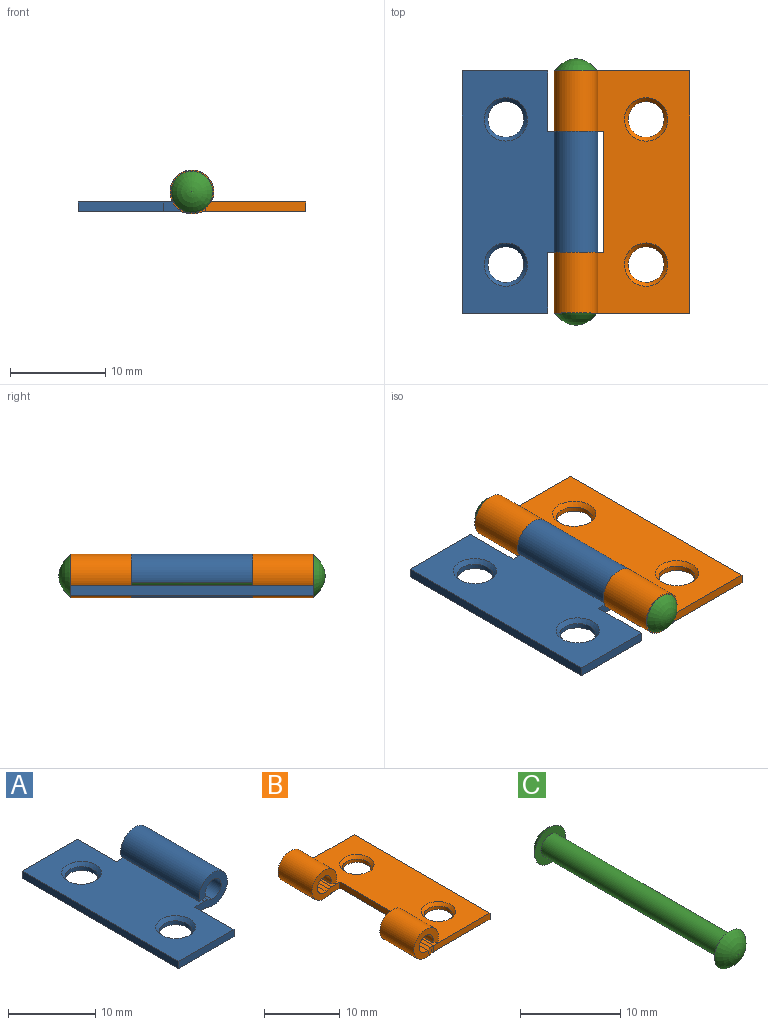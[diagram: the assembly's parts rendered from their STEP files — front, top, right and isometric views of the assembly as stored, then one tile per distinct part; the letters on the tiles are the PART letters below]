
ASSEMBLY  parts=3 mates=2
PART A: 20 faces, bbox 14.2x25.4x4.6 mm
  f0: cylinder r=2.3mm len=12.7mm, axis (0,1,0), area 154.7mm2, adj f1,f8,f13,f14
  f1: plane 12.7x0.95mm, normal (0.32,0,-0.95), area 12.7mm2, adj f0,f2,f13,f14
  f2: cylinder r=1.3mm len=12.7mm, axis (0,1,0), area 87.4mm2, adj f1,f3,f13,f14
  f3: plane 12.7x0.51mm, normal (0.26,0,0.97), area 6.7mm2, adj f2,f4,f13,f14
  f4: cylinder r=2.13mm len=12.7mm, axis (0,1,0), area 7.1mm2, adj f3,f5,f13,f14
  f5: plane 25.4x10.53mm, normal (0,0,1), area 214.9mm2, adj f4,f9,f10,f11,f12,f13,f14,f15
  f6: plane 25.4x10.53mm, normal (0,0,-1), area 225.2mm2, adj f7,f9,f10,f11,f12,f13,f14,f15
  f7: cylinder r=1.13mm len=12.7mm, axis (0,1,0), area 3.8mm2, adj f6,f8,f13,f14
  f8: plane 12.7x0.51mm, normal (-0.26,0,-0.97), area 6.7mm2, adj f0,f7,f13,f14
  f9: plane 8.95x1mm, normal (0,-1,0), area 8.9mm2, adj f5,f6,f11,f15
  f10: plane 8.95x1mm, normal (0,1,0), area 8.9mm2, adj f5,f6,f11,f12
  f11: plane 25.4x1mm, normal (-1,0,0), area 25.4mm2, adj f5,f6,f9,f10
  f12: plane 6.35x1mm, normal (1,0,0), area 6.3mm2, adj f5,f6,f10,f13
  f13: plane 5.28x4.6mm, normal (0,1,0), area 12.1mm2, adj f0,f1,f2,f3,f4,f5,f6,f7
  f14: plane 5.28x4.6mm, normal (0,-1,0), area 12.1mm2, adj f0,f1,f2,f3,f4,f5,f6,f7
  f15: plane 6.35x1mm, normal (1,0,0), area 6.4mm2, adj f5,f6,f9,f14
  f16: cylinder r=1.88mm len=3.76mm, axis (0,0,1), area 6.5mm2, adj f6,f17
  f17: cone r=2.27mm half-angle=41deg, axis (0,0,1), area 7.8mm2, adj f5,f16
  f18: cylinder r=1.88mm len=3.76mm, axis (0,0,1), area 6.5mm2, adj f6,f19
  f19: cone r=2.27mm half-angle=41deg, axis (0,0,1), area 7.8mm2, adj f5,f18
PART B: 32 faces, bbox 14.2x25.4x4.6 mm
  f0: cylinder r=2.3mm len=6.35mm, axis (0,-1,0), area 78.1mm2, adj f1,f6,f11,f26
  f1: plane 6.35x0.93mm, normal (-0.36,0,-0.93), area 6.3mm2, adj f0,f2,f11,f26
  f2: cylinder r=1.3mm len=6.35mm, axis (0,-1,0), area 44.1mm2, adj f1,f3,f11,f26
  f3: plane 6.35x0.51mm, normal (-0.26,0,0.97), area 3.4mm2, adj f2,f4,f8,f26
  f4: cylinder r=2.13mm len=6.35mm, axis (0,-1,0), area 3.5mm2, adj f3,f7,f18,f26
  f5: cylinder r=1.13mm len=6.35mm, axis (0,-1,0), area 1.9mm2, adj f6,f7,f20,f26
  f6: plane 6.35x0.51mm, normal (0.26,0,-0.97), area 3.4mm2, adj f0,f5,f8,f26
  f7: plane 1.04x0.55mm, normal (0,1,0), area 0.4mm2, adj f4,f5,f8,f23
  f8: plane 1.1x0.77mm, normal (0,1,0), area 0.5mm2, adj f3,f6,f7,f11
  f9: plane 1.04x0.55mm, normal (0,-1,0), area 0.4mm2, adj f10,f17,f21,f24
  f10: plane 10.54x1mm, normal (0,-1,0), area 10.5mm2, adj f9,f18,f19,f20
  f11: plane 4.6x4.6mm, normal (0,1,0), area 9.6mm2, adj f0,f1,f2,f8
  f12: plane 4.6x4.6mm, normal (0,-1,0), area 9.6mm2, adj f13,f14,f15,f24
  f13: cylinder r=2.3mm len=6.35mm, axis (0,-1,0), area 78.1mm2, adj f12,f14,f22,f27
  f14: plane 6.35x0.93mm, normal (-0.36,0,-0.93), area 6.3mm2, adj f12,f13,f15,f27
  f15: cylinder r=1.3mm len=6.35mm, axis (0,-1,0), area 44.1mm2, adj f12,f14,f16,f27
  f16: plane 6.35x0.51mm, normal (-0.26,0,0.97), area 3.4mm2, adj f15,f17,f24,f27
  f17: cylinder r=2.13mm len=6.35mm, axis (0,-1,0), area 3.5mm2, adj f9,f16,f18,f27
  f18: plane 25.4x10.54mm, normal (0,0,1), area 215.6mm2, adj f4,f10,f17,f19,f23,f25,f26,f27
  f19: plane 25.4x1mm, normal (1,0,0), area 25.4mm2, adj f10,f18,f20,f23
  f20: plane 25.4x10.54mm, normal (0,0,-1), area 225.9mm2, adj f5,f10,f19,f21,f23,f25,f26,f27
  f21: cylinder r=1.13mm len=6.35mm, axis (0,-1,0), area 1.9mm2, adj f9,f20,f22,f27
  f22: plane 6.35x0.51mm, normal (0.26,0,-0.97), area 3.4mm2, adj f13,f21,f24,f27
  f23: plane 10.54x1mm, normal (0,1,0), area 10.5mm2, adj f7,f18,f19,f20
  f24: plane 1.1x0.77mm, normal (0,-1,0), area 0.5mm2, adj f9,f12,f16,f22
  f25: plane 12.7x1mm, normal (-1,0,0), area 12.7mm2, adj f18,f20,f26,f27
  f26: plane 5.24x4.6mm, normal (0,-1,0), area 12.1mm2, adj f0,f1,f2,f3,f4,f5,f6,f18
  f27: plane 5.24x4.6mm, normal (0,1,0), area 12.1mm2, adj f13,f14,f15,f16,f17,f18,f20,f21
  f28: cylinder r=1.88mm len=3.76mm, axis (0,0,1), area 6.5mm2, adj f20,f29
  f29: cone r=2.27mm half-angle=41deg, axis (0,0,1), area 7.8mm2, adj f18,f28
  f30: cylinder r=1.88mm len=3.76mm, axis (0,0,1), area 6.5mm2, adj f20,f31
  f31: cone r=2.27mm half-angle=41deg, axis (0,0,1), area 7.8mm2, adj f18,f30
PART C: 5 faces, bbox 4.4x27.9x4.4 mm
  f0: cylinder r=1.3mm len=25.4mm, axis (0,1,0), area 207.5mm2, adj f1,f3
  f1: plane 4.38x4.38mm, normal (0,1,0), area 9.7mm2, adj f0,f2
  f2: revolved ~4.38x4.38mm, area 20mm2, adj f1
  f3: plane 4.38x4.38mm, normal (0,-1,0), area 9.7mm2, adj f0,f4
  f4: revolved ~4.38x4.38mm, area 20mm2, adj f3
PLACE A at identity fixed
PLACE B at identity
PLACE C at identity
MATE fastened C.f0 <-> B.f0  axis (0,1,0) through (3.06,-14.3,3.23)mm
MATE revolute B.f0 <-> A.f0  axis (0,-1,0) through (3.06,-1.6,3.23)mm
